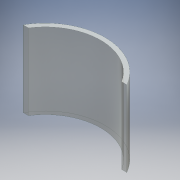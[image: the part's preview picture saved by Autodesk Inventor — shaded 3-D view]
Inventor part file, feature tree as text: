
AUTODESK INVENTOR PART (.ipt)
format: ipt  version: 2016 (Build 200138000, 138)  size: 103,936 bytes
history: native  units: mm
features: extrude x1, sketch x1
ambient origin geometry x8: Origin, YZ Plane, XZ Plane, XY Plane, X Axis, Y Axis, Z Axis, Center Point
bodies: Body1 (feature_tree)
feature tree (2):
  extrude  "押し出し2"  Depth=70.0mm TaperAngle=0.0deg
  sketch  "スケッチ2"
